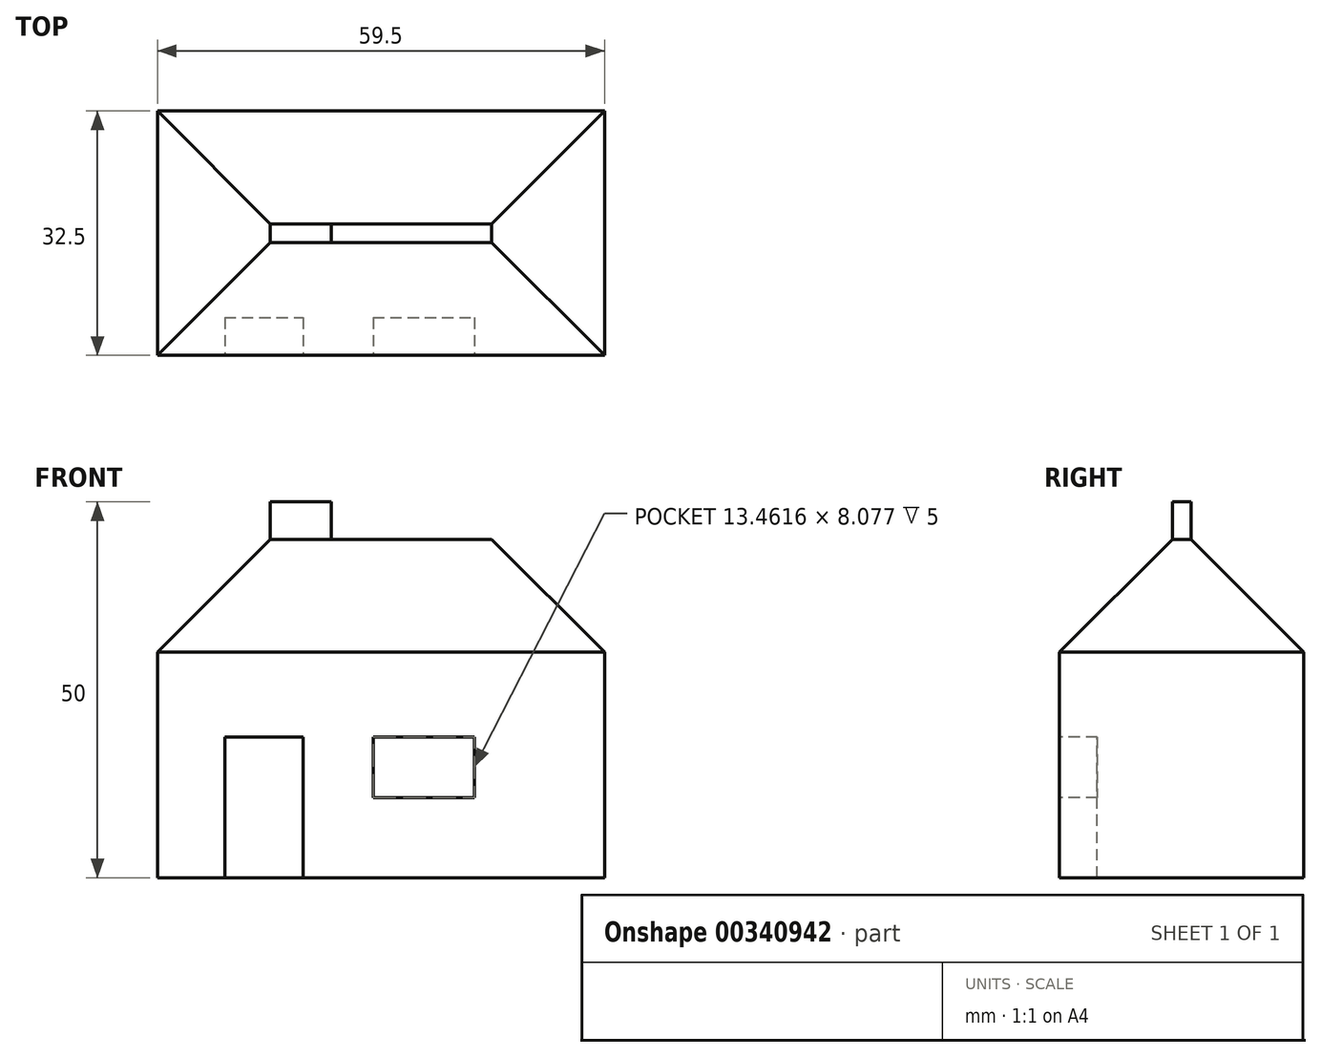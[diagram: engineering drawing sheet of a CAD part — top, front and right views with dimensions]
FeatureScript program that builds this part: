
annotation { "Feature Type Name" : "Feature", "Feature Type Description" : "" }
export const myFeature = defineFeature(function(context is Context, id is Id, definition is map)
    precondition{}
    {
        {
            var Q0;
            Q0=qCreatedBy(makeId("Top.planeOp"),FACE);
            var sketch = newSketch(context, id + "F0", { "sketchPlane" : qUnion([Q0])});
            skLineSegment(sketch, "E0.bottom", {"start": v(0, 0) * mm, "end": v(59.5, 0) * mm});
            skLineSegment(sketch, "E0.top", {"start": v(0, 32.5) * mm, "end": v(59.5, 32.5) * mm});
            skLineSegment(sketch, "E0.left", {"start": v(0, 0) * mm, "end": v(0, 32.5) * mm});
            skLineSegment(sketch, "E0.right", {"start": v(59.5, 0) * mm, "end": v(59.5, 32.5) * mm});
            skSolve(sketch);
        }
        {
            var Q0;
            Q0 = qSketchRegion(id + "F0", true);
            extrude(context, id + "F1", {"entities" : qUnion([Q0]), "depth" : 25 * mm});
        }
        {
            var Q0;
            Q0=makeQuery(id+"F1.opExtrude","CAP_FACE",FACE,{"disambiguationData":[OSD([sQuery(id+"F0.wireOp",EDGE,"E0.bottom"),sQuery(id+"F0.wireOp",EDGE,"E0.top"),sQuery(id+"F0.wireOp",EDGE,"E0.left"),sQuery(id+"F0.wireOp",EDGE,"E0.right")])],"isStart":false});
            var sketch = newSketch(context, id + "F2", { "sketchPlane" : qUnion([Q0])});
            skLineSegment(sketch, "E1", {"start": v(0, 32.5) * mm, "end": v(59.5, 32.5) * mm});
            skLineSegment(sketch, "E2", {"start": v(59.5, 32.5) * mm, "end": v(59.5, 0) * mm});
            skLineSegment(sketch, "E3", {"start": v(59.5, 0) * mm, "end": v(0, 0) * mm});
            skLineSegment(sketch, "E4", {"start": v(0, 0) * mm, "end": v(0, 32.5) * mm});
            skSolve(sketch);
        }
        {
            var Q0;
            Q0 = qSketchRegion(id + "F2", true);
            extrude(context, id + "F3", {"entities" : qUnion([Q0]), "operationType" : NewBodyOperationType.ADD, "depth" : 20 * mm});
        }
        {
            var Q0;
            Q0=makeQuery(id+"F3.opExtrude","CAP_EDGE",EDGE,{"disambiguationData":[OSD([sQuery(id+"F2.wireOp",EDGE,"E4")])],"isStart":false});
            var Q1;
            Q1=makeQuery(id+"F3.opExtrude","CAP_EDGE",EDGE,{"disambiguationData":[OSD([sQuery(id+"F2.wireOp",EDGE,"E2")])],"isStart":false});
            var Q2;
            Q2=makeQuery(id+"F3.opExtrude","CAP_EDGE",EDGE,{"disambiguationData":[OSD([sQuery(id+"F2.wireOp",EDGE,"E3")])],"isStart":false});
            var Q3;
            Q3=makeQuery(id+"F3.opExtrude","CAP_EDGE",EDGE,{"disambiguationData":[OSD([sQuery(id+"F2.wireOp",EDGE,"E1")])],"isStart":false});
            chamfer(context, id + "F4", {"entities" : qUnion([Q0, Q1, Q2, Q3]), "width" : 15 * mm, "tangentPropagation" : true});
        }
        {
            var Q0;
            Q0=makeQuery(id+"F3.boolean.opBoolean","MERGE",FACE,{"derivedFrom":[makeQuery(id+"F1.opExtrude","SWEPT_FACE",FACE,{"disambiguationData":[OSD([sQuery(id+"F0.wireOp",EDGE,"E0.bottom")])]}),makeQuery(id+"F3.opExtrude","SWEPT_FACE",FACE,{"disambiguationData":[OSD([sQuery(id+"F2.wireOp",EDGE,"E3")])]})]});
            var sketch = newSketch(context, id + "F5", { "sketchPlane" : qUnion([Q0])});
            skLineSegment(sketch, "E5.bottom", {"start": v(8.94, 0) * mm, "end": v(19.41, 0) * mm});
            skLineSegment(sketch, "E5.top", {"start": v(8.94, 18.74) * mm, "end": v(19.41, 18.74) * mm});
            skLineSegment(sketch, "E5.left", {"start": v(8.94, 0) * mm, "end": v(8.94, 18.74) * mm});
            skLineSegment(sketch, "E5.right", {"start": v(19.41, 0) * mm, "end": v(19.41, 18.74) * mm});
            skLineSegment(sketch, "E6.bottom", {"start": v(28.69, 18.74) * mm, "end": v(42.15, 18.74) * mm});
            skLineSegment(sketch, "E6.top", {"start": v(28.69, 10.66) * mm, "end": v(42.15, 10.66) * mm});
            skLineSegment(sketch, "E6.left", {"start": v(28.69, 18.74) * mm, "end": v(28.69, 10.66) * mm});
            skLineSegment(sketch, "E6.right", {"start": v(42.15, 18.74) * mm, "end": v(42.15, 10.66) * mm});
            skSolve(sketch);
        }
        {
            var Q0;
            Q0 = qSketchRegion(id + "F5", true);
            extrude(context, id + "F6", {"entities" : qUnion([Q0]), "operationType" : NewBodyOperationType.REMOVE, "oppositeDirection" : true, "depth" : 5 * mm});
        }
        {
            var Q0;
            Q0=makeQuery(id+"F3.opExtrude","CAP_FACE",FACE,{"disambiguationData":[OSD([sQuery(id+"F2.wireOp",EDGE,"E1"),sQuery(id+"F2.wireOp",EDGE,"E2"),sQuery(id+"F2.wireOp",EDGE,"E3"),sQuery(id+"F2.wireOp",EDGE,"E4")])],"isStart":false});
            var sketch = newSketch(context, id + "F7", { "sketchPlane" : qUnion([Q0])});
            skLineSegment(sketch, "E7.bottom", {"start": v(15, 17.5) * mm, "end": v(23.15, 17.5) * mm});
            skLineSegment(sketch, "E7.top", {"start": v(15, 15) * mm, "end": v(23.15, 15) * mm});
            skLineSegment(sketch, "E7.left", {"start": v(15, 17.5) * mm, "end": v(15, 15) * mm});
            skLineSegment(sketch, "E7.right", {"start": v(23.15, 17.5) * mm, "end": v(23.15, 15) * mm});
            skSolve(sketch);
        }
        {
            var Q0;
            Q0=makeQuery(id+"F7.imprint","IMPRINT",FACE,{"disambiguationData":[TD([[makeQuery(id+"F7.imprint","IMPRINT",EDGE,{"derivedFrom":sQuery(id+"F7.wireOp",EDGE,"E7.bottom")}),1.0]])]});
            extrude(context, id + "F8", {"entities" : qUnion([Q0]), "operationType" : NewBodyOperationType.ADD, "depth" : 5 * mm});
        }
    });
